# Revit family: Rohrschelle Trabant, M 8-M10, o.D.
name_source: partatom
category: HLS-Bauteile
revit_build: Autodesk Revit 2017 (Build: 20190507_1515(x64)
units: mm (PartAtom-declared; Revit-internal decimal feet)

## family parameters
Arbeitsebenenbasiert = Ja
Beim Laden mit Abzugskörper schneiden = Nein
Bemaßung runder Anschluss = Durchmesser verwenden
Gemeinsam genutzt = Ja
Immer vertikal = Nein
Raumberechnungspunkt = Nein
Teiletyp = Normal

## types (14) — shared parameters
Anschluss = M8/M10
Bauart = zweiteilig
DVS = 5 mm  [stored 0.0164042 ft]
Fabrikat = MEFA
Firma = MEFA Befestigungs- und Montagesysteme GmbH
H1 = 2 mm  [stored 0.00656168 ft]
HGA = 17 mm
Material = Stahl
Materialname = DD11
Mengeneinheit = St
Oberflaeche = galvanisch verzinkt
Verschluss = Rastverschluss
Verschluss-Schraube = M6
Vorgabe-Ansicht = 1219 mm
max. zul. Last horizontal = 0.00 kN
max. zul. Last vertikal = 0.00 kN
zero-valued in all types: DS, Nennweite DN Rohr, Rohraußendurchmesser, Stärke Material

## per-type parameters (varying)
- Trabant, Ø 21- 24, M8/M10, o.D.: A=18 mm  [stored 0.0590551 ft]; AB=3 mm  [stored 0.00984252 ft]; Anschlußhöhe=18 mm; Artikelnummer=042615201; B=59 mm; Breite=59 mm; D=24 mm  [stored 0.0787402 ft]; D0=24 mm  [stored 0.0787402 ft]; DF1=17 mm; DF2=16 mm  [stored 0.0524934 ft]; Dmax=24 mm  [stored 0.0787402 ft]; Dmin=21 mm  [stored 0.0688976 ft]; EAN=4250928457905; Gewicht=0.05 kg; Gewicht pro Bauteil=0.05 kg; H=43 mm  [stored 0.141076 ft]; H2=4 mm  [stored 0.0131234 ft]; Kurztext1=Rohrschelle Trabant 20x1,0; Kurztext2=21 - 24 mm M8/M10; MB=20 mm  [stored 0.0656168 ft]; MD=1 mm  [stored 0.00328084 ft]; Materialmaße=20x1,0 mm; R=12 mm  [stored 0.0393701 ft]; RM=15 mm  [stored 0.0492126 ft]; S=42 mm  [stored 0.137795 ft]; max. Höhe=43 mm  [stored 0.141076 ft]; max. Rohraußendurchmesser=24 mm  [stored 0.0787402 ft]; max. zul. Last=0.29 kN; min. Rohraußendurchmesser=21 mm  [stored 0.0688976 ft]; vpe=100 St
- Trabant, Ø 25- 29, M8/M10, o.D.: A=18 mm  [stored 0.0590551 ft]; AB=4 mm  [stored 0.0131234 ft]; Anschlußhöhe=18 mm; Artikelnummer=042620201; B=64 mm; Breite=64 mm; D=29 mm  [stored 0.0951444 ft]; D0=29 mm  [stored 0.0951444 ft]; DF1=17 mm; DF2=16 mm  [stored 0.0524934 ft]; Dmax=29 mm  [stored 0.0951444 ft]; Dmin=25 mm  [stored 0.082021 ft]; EAN=4250928457929; Gewicht=0.05 kg; Gewicht pro Bauteil=0.05 kg; H=48 mm  [stored 0.15748 ft]; H2=5 mm  [stored 0.0164042 ft]; Kurztext1=Rohrschelle Trabant 20x1,0; Kurztext2=25 - 29 mm M8/M10; MB=20 mm  [stored 0.0656168 ft]; MD=1 mm  [stored 0.00328084 ft]; Materialmaße=20x1,0 mm; R=15 mm  [stored 0.0492126 ft]; RM=18 mm  [stored 0.0590551 ft]; S=47 mm  [stored 0.154199 ft]; max. Höhe=48 mm  [stored 0.15748 ft]; max. Rohraußendurchmesser=29 mm  [stored 0.0951444 ft]; max. zul. Last=0.29 kN; min. Rohraußendurchmesser=25 mm  [stored 0.082021 ft]; vpe=100 St
- Trabant, Ø 30- 34, M8/M10, o.D.: A=18 mm  [stored 0.0590551 ft]; AB=4 mm  [stored 0.0131234 ft]; Anschlußhöhe=18 mm; Artikelnummer=042625201; B=69 mm; Breite=69 mm; D=34 mm  [stored 0.111549 ft]; D0=34 mm  [stored 0.111549 ft]; DF1=17 mm; DF2=16 mm  [stored 0.0524934 ft]; Dmax=34 mm  [stored 0.111549 ft]; Dmin=30 mm  [stored 0.0984252 ft]; EAN=4250928457936; Gewicht=0.05 kg; Gewicht pro Bauteil=0.05 kg; H=53 mm  [stored 0.173885 ft]; H2=5 mm  [stored 0.0164042 ft]; Kurztext1=Rohrschelle Trabant 20x1,0; Kurztext2=30 - 34 mm M8/M10; MB=20 mm  [stored 0.0656168 ft]; MD=1 mm  [stored 0.00328084 ft]; Materialmaße=20x1,0 mm; R=17 mm; RM=20 mm  [stored 0.0656168 ft]; S=52 mm  [stored 0.170604 ft]; max. Höhe=53 mm  [stored 0.173885 ft]; max. Rohraußendurchmesser=34 mm  [stored 0.111549 ft]; max. zul. Last=0.29 kN; min. Rohraußendurchmesser=30 mm  [stored 0.0984252 ft]; vpe=100 St
- Trabant, Ø 35- 39, M8/M10, o.D.: A=18 mm  [stored 0.0590551 ft]; AB=4 mm  [stored 0.0131234 ft]; Anschlußhöhe=18 mm; Artikelnummer=042630201; B=74 mm; Breite=75 mm; D=39 mm  [stored 0.127953 ft]; D0=39 mm  [stored 0.127953 ft]; DF1=17 mm; DF2=16 mm  [stored 0.0524934 ft]; Dmax=39 mm  [stored 0.127953 ft]; Dmin=35 mm  [stored 0.114829 ft]; EAN=4250928457943; Gewicht=0.05 kg; Gewicht pro Bauteil=0.05 kg; H=58 mm; H2=5 mm  [stored 0.0164042 ft]; Kurztext1=Rohrschelle Trabant 20x1,0; Kurztext2=35 - 39 mm M8/M10; MB=20 mm  [stored 0.0656168 ft]; MD=1 mm  [stored 0.00328084 ft]; Materialmaße=20x1,0 mm; R=20 mm  [stored 0.0656168 ft]; RM=23 mm; S=57 mm; max. Höhe=58 mm; max. Rohraußendurchmesser=39 mm  [stored 0.127953 ft]; max. zul. Last=0.29 kN; min. Rohraußendurchmesser=35 mm  [stored 0.114829 ft]; vpe=100 St
- Trabant, Ø 41- 48, M8/M10, o.D.: A=18 mm  [stored 0.0590551 ft]; AB=7 mm  [stored 0.0229659 ft]; Anschlußhöhe=18 mm; Artikelnummer=042637201; B=83 mm; Breite=91 mm; D=48 mm  [stored 0.15748 ft]; D0=48 mm  [stored 0.15748 ft]; DF1=17 mm; DF2=16 mm  [stored 0.0524934 ft]; Dmax=48 mm  [stored 0.15748 ft]; Dmin=41 mm  [stored 0.134514 ft]; EAN=4250928457950; Gewicht=0.06 kg; Gewicht pro Bauteil=0.06 kg; H=67 mm; H2=6 mm  [stored 0.019685 ft]; Kurztext1=Rohrschelle Trabant 20x1,0; Kurztext2=41 - 48 mm M8/M10; MB=20 mm  [stored 0.0656168 ft]; MD=1 mm  [stored 0.00328084 ft]; Materialmaße=20x1,0 mm; R=24 mm  [stored 0.0787402 ft]; RM=29 mm  [stored 0.0951444 ft]; S=66 mm; max. Höhe=67 mm; max. Rohraußendurchmesser=48 mm  [stored 0.15748 ft]; max. zul. Last=0.29 kN; min. Rohraußendurchmesser=41 mm  [stored 0.134514 ft]; vpe=100 St
- Trabant, Ø 51- 55, M8/M10, o.D.: A=19 mm; AB=4 mm  [stored 0.0131234 ft]; Anschlußhöhe=18 mm; Artikelnummer=042646201; B=92 mm; Breite=92 mm; D=55 mm; D0=55 mm; DF1=18 mm  [stored 0.0590551 ft]; DF2=16 mm  [stored 0.0524934 ft]; Dmax=55 mm; Dmin=51 mm  [stored 0.167323 ft]; EAN=4250928457967; Gewicht=0.08 kg; Gewicht pro Bauteil=0.08 kg; H=75 mm; H2=5 mm  [stored 0.0164042 ft]; Kurztext1=Rohrschelle Trabant 20x1,5; Kurztext2=51 - 55 mm M8/M10; MB=20 mm  [stored 0.0656168 ft]; MD=2 mm  [stored 0.00656168 ft]; Materialmaße=20x1,5 mm; R=28 mm; RM=31 mm  [stored 0.101706 ft]; S=74 mm; max. Höhe=75 mm; max. Rohraußendurchmesser=55 mm; max. zul. Last=0.89 kN; min. Rohraußendurchmesser=51 mm  [stored 0.167323 ft]; vpe=50 St
- Trabant, Ø 57- 61, M8/M10, o.D.: A=19 mm; AB=4 mm  [stored 0.0131234 ft]; Anschlußhöhe=18 mm; Artikelnummer=042652201; B=98 mm; Breite=98 mm; D=61 mm; D0=61 mm; DF1=18 mm  [stored 0.0590551 ft]; DF2=16 mm  [stored 0.0524934 ft]; Dmax=61 mm; Dmin=57 mm; EAN=4250928457974; Gewicht=0.08 kg; Gewicht pro Bauteil=0.08 kg; H=81 mm; H2=5 mm  [stored 0.0164042 ft]; Kurztext1=Rohrschelle Trabant 20x1,5; Kurztext2=57 - 61 mm M8/M10; MB=20 mm  [stored 0.0656168 ft]; MD=2 mm  [stored 0.00656168 ft]; Materialmaße=20x1,5 mm; R=31 mm  [stored 0.101706 ft]; RM=34 mm  [stored 0.111549 ft]; S=80 mm; max. Höhe=81 mm; max. Rohraußendurchmesser=61 mm; max. zul. Last=0.89 kN; min. Rohraußendurchmesser=57 mm; vpe=50 St
- Trabant, Ø 63- 67, M8/M10, o.D.: A=19 mm; AB=4 mm  [stored 0.0131234 ft]; Anschlußhöhe=18 mm; Artikelnummer=042658201; B=104 mm; Breite=104 mm; D=67 mm; D0=67 mm; DF1=18 mm  [stored 0.0590551 ft]; DF2=16 mm  [stored 0.0524934 ft]; Dmax=67 mm; Dmin=63 mm; EAN=4250928457981; Gewicht=0.09 kg; Gewicht pro Bauteil=0.09 kg; H=87 mm; H2=5 mm  [stored 0.0164042 ft]; Kurztext1=Rohrschelle Trabant 20x1,5; Kurztext2=63 - 67 mm M8/M10; MB=20 mm  [stored 0.0656168 ft]; MD=2 mm  [stored 0.00656168 ft]; Materialmaße=20x1,5 mm; R=34 mm  [stored 0.111549 ft]; RM=37 mm  [stored 0.121391 ft]; S=86 mm; max. Höhe=87 mm; max. Rohraußendurchmesser=67 mm; max. zul. Last=0.89 kN; min. Rohraußendurchmesser=63 mm; vpe=50 St
- Trabant, Ø 69- 74, M8/M10, o.D.: A=19 mm; AB=5 mm  [stored 0.0164042 ft]; Anschlußhöhe=18 mm; Artikelnummer=042665201; B=111 mm; Breite=111 mm; D=74 mm; D0=74 mm; DF1=18 mm  [stored 0.0590551 ft]; DF2=16 mm  [stored 0.0524934 ft]; Dmax=74 mm; Dmin=69 mm; EAN=4250928457998; Gewicht=0.09 kg; Gewicht pro Bauteil=0.09 kg; H=94 mm; H2=6 mm  [stored 0.019685 ft]; Kurztext1=Rohrschelle Trabant 20x1,5; Kurztext2=69 - 74 mm M8/M10; MB=20 mm  [stored 0.0656168 ft]; MD=2 mm  [stored 0.00656168 ft]; Materialmaße=20x1,5 mm; R=37 mm  [stored 0.121391 ft]; RM=41 mm  [stored 0.134514 ft]; S=93 mm; max. Höhe=94 mm; max. Rohraußendurchmesser=74 mm; max. zul. Last=0.89 kN; min. Rohraußendurchmesser=69 mm; vpe=50 St
- Trabant, Ø 76- 85, M8/M10, o.D.: A=19 mm; AB=9 mm  [stored 0.0295276 ft]; Anschlußhöhe=18 mm; Artikelnummer=042672201; B=122 mm; Breite=122 mm; D=85 mm; D0=85 mm; DF1=18 mm  [stored 0.0590551 ft]; DF2=16 mm  [stored 0.0524934 ft]; Dmax=85 mm; Dmin=76 mm; EAN=4250928458001; Gewicht=0.12 kg; Gewicht pro Bauteil=0.12 kg; H=105 mm; H2=8 mm  [stored 0.0262467 ft]; Kurztext1=Rohrschelle Trabant 25x1,5; Kurztext2=76 - 85 mm M8/M10; MB=25 mm  [stored 0.082021 ft]; MD=2 mm  [stored 0.00656168 ft]; Materialmaße=25x1,5 mm; R=43 mm  [stored 0.141076 ft]; RM=49 mm; S=104 mm; max. Höhe=104 mm; max. Rohraußendurchmesser=85 mm; max. zul. Last=0.89 kN; min. Rohraußendurchmesser=76 mm; vpe=50 St
- Trabant, Ø 84- 90, M8/M10, o.D.: A=19 mm; AB=6 mm  [stored 0.019685 ft]; Anschlußhöhe=18 mm; Artikelnummer=042677201; B=127 mm; Breite=127 mm; D=90 mm; D0=90 mm; DF1=18 mm  [stored 0.0590551 ft]; DF2=16 mm  [stored 0.0524934 ft]; Dmax=90 mm; Dmin=84 mm; EAN=4250928458018; Gewicht=0.13 kg; Gewicht pro Bauteil=0.13 kg; H=110 mm; H2=6 mm  [stored 0.019685 ft]; Kurztext1=Rohrschelle Trabant 25x1,5; Kurztext2=84 - 90 mm M8/M10; MB=25 mm  [stored 0.082021 ft]; MD=2 mm  [stored 0.00656168 ft]; Materialmaße=25x1,5 mm; R=45 mm  [stored 0.147638 ft]; RM=50 mm  [stored 0.164042 ft]; S=109 mm; max. Höhe=109 mm; max. Rohraußendurchmesser=90 mm; max. zul. Last=0.89 kN; min. Rohraußendurchmesser=84 mm; vpe=50 St
- Trabant, Ø 94- 97, M8/M10, o.D.: A=19 mm; AB=3 mm  [stored 0.00984252 ft]; Anschlußhöhe=18 mm; Artikelnummer=0426902; B=134 mm; Breite=134 mm; D=97 mm; D0=97 mm; DF1=17 mm; DF2=16 mm  [stored 0.0524934 ft]; Dmax=97 mm; Dmin=94 mm; EAN=4250928458025; Gewicht=0.15 kg; Gewicht pro Bauteil=0.15 kg; H=118 mm; H2=5 mm  [stored 0.0164042 ft]; Kurztext1=Rohrschelle Trabant 25x2,0; Kurztext2=94 - 97 mm M8/M10; MB=25 mm  [stored 0.082021 ft]; MD=2 mm  [stored 0.00656168 ft]; Materialmaße=25x2,0 mm; R=49 mm; RM=52 mm  [stored 0.170604 ft]; S=117 mm; max. Höhe=119 mm; max. Rohraußendurchmesser=97 mm; max. zul. Last=1.50 kN; min. Rohraußendurchmesser=94 mm; vpe=50 St
- Trabant, Ø106-110, M8/M10, o.D.: A=20 mm  [stored 0.0656168 ft]; AB=4 mm  [stored 0.0131234 ft]; Anschlußhöhe=22 mm; Artikelnummer=0427022; B=153 mm; Breite=153 mm; D=110 mm; D0=110 mm; DF1=17 mm; DF2=21 mm  [stored 0.0688976 ft]; Dmax=110 mm; Dmin=106 mm; EAN=4250928458032; Gewicht=0.23 kg; Gewicht pro Bauteil=0.23 kg; H=132 mm; H2=6 mm  [stored 0.019685 ft]; Kurztext1=Rohrschelle Trabant 25x2,5; Kurztext2=106 - 110 mm M8/M10; MB=25 mm  [stored 0.082021 ft]; MD=3 mm  [stored 0.00984252 ft]; Materialmaße=25x2,5 mm; R=55 mm; RM=60 mm; S=136 mm; max. Höhe=136 mm; max. Rohraußendurchmesser=110 mm; max. zul. Last=1.90 kN; min. Rohraußendurchmesser=106 mm; vpe=50 St
- Trabant, Ø114-122, M8/M10, o.D.: A=20 mm  [stored 0.0656168 ft]; AB=8 mm  [stored 0.0262467 ft]; Anschlußhöhe=22 mm; Artikelnummer=04272142; B=165 mm; Breite=166 mm; D=122 mm; D0=122 mm; DF1=17 mm; DF2=21 mm  [stored 0.0688976 ft]; Dmax=122 mm; Dmin=114 mm; EAN=4250928458049; Gewicht=0.24 kg; Gewicht pro Bauteil=0.24 kg; H=144 mm; H2=8 mm  [stored 0.0262467 ft]; Kurztext1=Rohrschelle Trabant 25x2,5; Kurztext2=114 - 122 mm M8/M10; MB=25 mm  [stored 0.082021 ft]; MD=3 mm  [stored 0.00984252 ft]; Materialmaße=25x2,5 mm; R=61 mm; RM=68 mm; S=148 mm; max. Höhe=148 mm; max. Rohraußendurchmesser=122 mm; max. zul. Last=1.90 kN; min. Rohraußendurchmesser=114 mm; vpe=50 St

note: [stored X ft] marks values corroborated as IEEE doubles in the binary element streams (Revit-internal decimal feet)

## geometry (parser evidence)
native form markers: Sweep x3
no freeform markers — native parametric forms only
